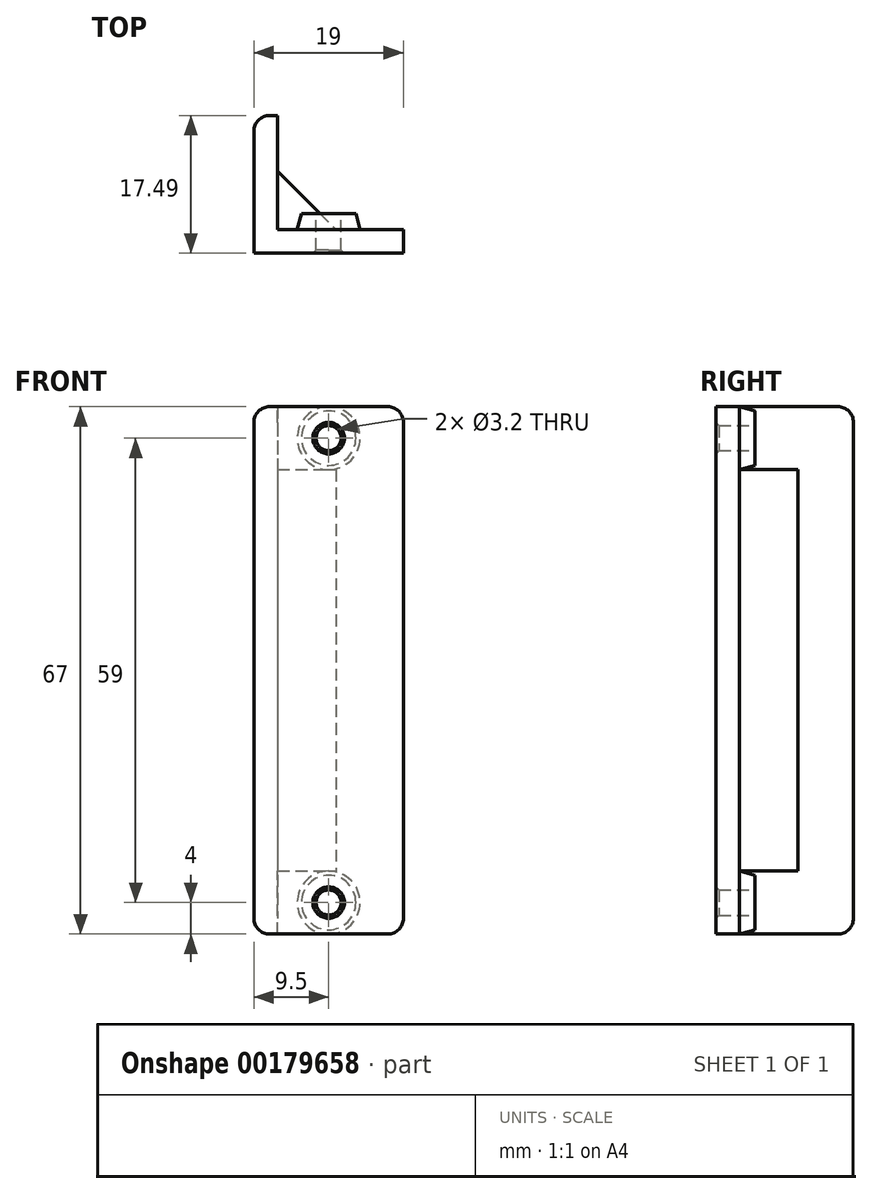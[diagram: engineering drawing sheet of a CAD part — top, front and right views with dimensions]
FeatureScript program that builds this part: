
annotation { "Feature Type Name" : "Feature", "Feature Type Description" : "" }
export const myFeature = defineFeature(function(context is Context, id is Id, definition is map)
    precondition{}
    {
        {
            var Q0;
            Q0=qCreatedBy(makeId("Top.planeOp"),FACE);
            var sketch = newSketch(context, id + "F0", { "sketchPlane" : qUnion([Q0])});
            skLineSegment(sketch, "E0", {"start": v(19, 0) * mm, "end": v(0, 0) * mm});
            skLineSegment(sketch, "E1", {"start": v(0, 0) * mm, "end": v(0, 17.49) * mm});
            skLineSegment(sketch, "E2", {"start": v(0, 17.49) * mm, "end": v(3, 17.49) * mm});
            skLineSegment(sketch, "E3", {"start": v(3, 17.49) * mm, "end": v(3, 10.42) * mm});
            skLineSegment(sketch, "E4", {"start": v(3, 10.42) * mm, "end": v(10.42, 3) * mm});
            skLineSegment(sketch, "E5", {"start": v(10.42, 3) * mm, "end": v(19, 3) * mm});
            skLineSegment(sketch, "E6", {"start": v(19, 3) * mm, "end": v(19, 0) * mm});
            skLineSegment(sketch, "E7", {"start": v(9.5, 10.11) * mm, "end": v(9.5, -4.35) * mm, "construction": true});
            skPoint(sketch, "E8", {"position": v(9.5, 0) * mm});
            skSolve(sketch);
        }
        {
            var Q0;
            Q0=qSketchRegion(id+"F0",true);
            extrude(context, id + "F1", {"entities" : qUnion([Q0]), "depth" : 25.5 * mm});
        }
        {
            var Q0;
            Q0=makeQuery(id+"F1.opExtrude","CAP_FACE",FACE,{"disambiguationData":[OSD([sQuery(id+"F0.wireOp",EDGE,"E0"),sQuery(id+"F0.wireOp",EDGE,"E1"),sQuery(id+"F0.wireOp",EDGE,"E2"),sQuery(id+"F0.wireOp",EDGE,"E3"),sQuery(id+"F0.wireOp",EDGE,"E4"),sQuery(id+"F0.wireOp",EDGE,"E5"),sQuery(id+"F0.wireOp",EDGE,"E6")])],"isStart":false});
            var sketch = newSketch(context, id + "F2", { "sketchPlane" : qUnion([Q0])});
            skLineSegment(sketch, "E9", {"start": v(19, 3) * mm, "end": v(3, 3) * mm});
            skLineSegment(sketch, "E10", {"start": v(3, 3) * mm, "end": v(3, 17.49) * mm});
            skSolve(sketch);
        }
        {
            var Q0;
            Q0=makeQuery(id+"F2.imprint","IMPRINT",FACE,{"disambiguationData":[TD([[makeQuery(id+"F2.imprint","IMPRINT",EDGE,{"derivedFrom":makeQuery(id+"F1.opExtrude","CAP_EDGE",EDGE,{"disambiguationData":[OSD([sQuery(id+"F0.wireOp",EDGE,"E0")])],"isStart":false})}),-1.0]])]});
            extrude(context, id + "F3", {"entities" : qUnion([Q0]), "operationType" : NewBodyOperationType.ADD, "depth" : 8 * mm});
        }
        {
            var Q0;
            Q0=makeQuery(id+"F3.boolean.opBoolean","MERGE",FACE,{"derivedFrom":[makeQuery(id+"F1.opExtrude","SWEPT_FACE",FACE,{"disambiguationData":[OSD([sQuery(id+"F0.wireOp",EDGE,"E5")])]}),makeQuery(id+"F3.opExtrude","SWEPT_FACE",FACE,{"disambiguationData":[OSD([sQuery(id+"F2.wireOp",EDGE,"E9")])]})]});
            var sketch = newSketch(context, id + "F4", { "sketchPlane" : qUnion([Q0])});
            skLineSegment(sketch, "E11.0", {"start": v(0, 33.5) * mm, "end": v(0, 0) * mm, "construction": true});
            skPoint(sketch, "E12", {"position": v(-3, 29.5) * mm});
            skLineSegment(sketch, "E13", {"start": v(0, 29.5) * mm, "end": v(-19, 29.5) * mm, "construction": true});
            skPoint(sketch, "E14", {"position": v(-9.5, 29.5) * mm});
            skCircle(sketch, "E15", {"center": v(-9.5, 29.5) * mm, "radius": 4 * mm});
            skSolve(sketch);
        }
        {
            var Q0;
            Q0=qSketchRegion(id+"F4",true);
            extrude(context, id + "F5", {"entities" : qUnion([Q0]), "operationType" : NewBodyOperationType.ADD, "depth" : 2 * mm, "hasDraft" : true, "draftAngle" : 15 * degree, "draftPullDirection" : true});
        }
        {
            var Q0;
            Q0=makeQuery(id+"F5.opExtrude","CAP_FACE",FACE,{"disambiguationData":[OSD([sQuery(id+"F4.wireOp",EDGE,"E15")])],"isStart":false});
            var sketch = newSketch(context, id + "F6", { "sketchPlane" : qUnion([Q0])});
            skCircle(sketch, "E16.0", {"center": v(-9.5, 29.5) * mm, "radius": 3.46 * mm, "construction": true});
            skCircle(sketch, "E17", {"center": v(-9.5, 29.5) * mm, "radius": 1.6 * mm});
            skSolve(sketch);
        }
        {
            var Q0;
            Q0=qSketchRegion(id+"F6",true);
            extrude(context, id + "F7", {"entities" : qUnion([Q0]), "operationType" : NewBodyOperationType.REMOVE, "endBound" : BoundingType.THROUGH_ALL, "oppositeDirection" : true, "depth" : 25 * mm});
        }
        {
            var Q0;
            {var subQ0=sQuery(id+"F0.wireOp",EDGE,"E0");Q0=makeQuery(id+"F7.boolean.opBoolean","INTERSECT",EDGE,{"derivedFrom":[makeQuery(id+"F3.boolean.opBoolean","MERGE",FACE,{"derivedFrom":[makeQuery(id+"F1.opExtrude","SWEPT_FACE",FACE,{"disambiguationData":[OSD([subQ0])]}),makeQuery(id+"F3.opExtrude","SWEPT_FACE",FACE,{"disambiguationData":[OSD([subQ0])]})]}),makeQuery(id+"F7.opExtrude","SWEPT_FACE",FACE,{"disambiguationData":[OSD([sQuery(id+"F6.wireOp",EDGE,"E17")])]})]});}
            chamfer(context, id + "F8", {"entities" : qUnion([Q0]), "width" : 0.4 * mm});
        }
        {
            var Q0;
            Q0=makeQuery(id+"F1.opExtrude","SWEPT_BODY",BODY,{"disambiguationData":[OSD([sQuery(id+"F0.wireOp",EDGE,"E0"),sQuery(id+"F0.wireOp",EDGE,"E1"),sQuery(id+"F0.wireOp",EDGE,"E2"),sQuery(id+"F0.wireOp",EDGE,"E3"),sQuery(id+"F0.wireOp",EDGE,"E4"),sQuery(id+"F0.wireOp",EDGE,"E5"),sQuery(id+"F0.wireOp",EDGE,"E6")])]});
            var Q1;
            Q1=qCreatedBy(makeId("Top.planeOp"),FACE);
            mirror(context, id + "F9", {"operationType" : NewBodyOperationType.ADD, "entities" : qUnion([Q0]), "mirrorPlane" : qUnion([Q1])});
        }
        {
            var Q0;
            {var subQ0=sQuery(id+"F0.wireOp",EDGE,"E2");var subQ1=sQuery(id+"F0.wireOp",EDGE,"E1");var subQ2=makeQuery(id+"F3.boolean.opBoolean","MERGE",EDGE,{"derivedFrom":[makeQuery(id+"F1.opExtrude","SWEPT_EDGE",EDGE,{"disambiguationData":[OSD([subQ1,subQ0])]}),makeQuery(id+"F3.opExtrude","SWEPT_EDGE",EDGE,{"disambiguationData":[OSD([subQ1,subQ0])]})]});Q0=makeQuery(id+"F9.boolean.opBoolean","MERGE",EDGE,{"derivedFrom":[subQ2,makeQuery(id+"F9.opPattern","COPY",EDGE,{"derivedFrom":subQ2,"instanceName":"1"})]});}
            var Q1;
            Q1=makeQuery(id+"F9.opPattern","COPY",EDGE,{"derivedFrom":makeQuery(id+"F3.opExtrude","CAP_EDGE",EDGE,{"disambiguationData":[OSD([sQuery(id+"F0.wireOp",EDGE,"E1")])],"isStart":false}),"instanceName":"1"});
            var Q2;
            Q2=makeQuery(id+"F9.opPattern","COPY",EDGE,{"derivedFrom":makeQuery(id+"F3.opExtrude","CAP_EDGE",EDGE,{"disambiguationData":[OSD([sQuery(id+"F0.wireOp",EDGE,"E2")])],"isStart":false}),"instanceName":"1"});
            var Q3;
            Q3=makeQuery(id+"F3.opExtrude","CAP_EDGE",EDGE,{"disambiguationData":[OSD([sQuery(id+"F0.wireOp",EDGE,"E2")])],"isStart":false});
            var Q4;
            Q4=makeQuery(id+"F3.opExtrude","CAP_EDGE",EDGE,{"disambiguationData":[OSD([sQuery(id+"F0.wireOp",EDGE,"E1")])],"isStart":false});
            var Q5;
            Q5=makeQuery(id+"F3.opExtrude","CAP_EDGE",EDGE,{"disambiguationData":[OSD([sQuery(id+"F0.wireOp",EDGE,"E6")])],"isStart":false});
            var Q6;
            Q6=makeQuery(id+"F9.opPattern","COPY",EDGE,{"derivedFrom":makeQuery(id+"F3.opExtrude","CAP_EDGE",EDGE,{"disambiguationData":[OSD([sQuery(id+"F0.wireOp",EDGE,"E6")])],"isStart":false}),"instanceName":"1"});
            fillet(context, id + "F10", {"entities" : qUnion([Q0, Q1, Q2, Q3, Q4, Q5, Q6]), "radius" : 2 * mm, "allowEdgeOverflow" : false});
        }
    });
